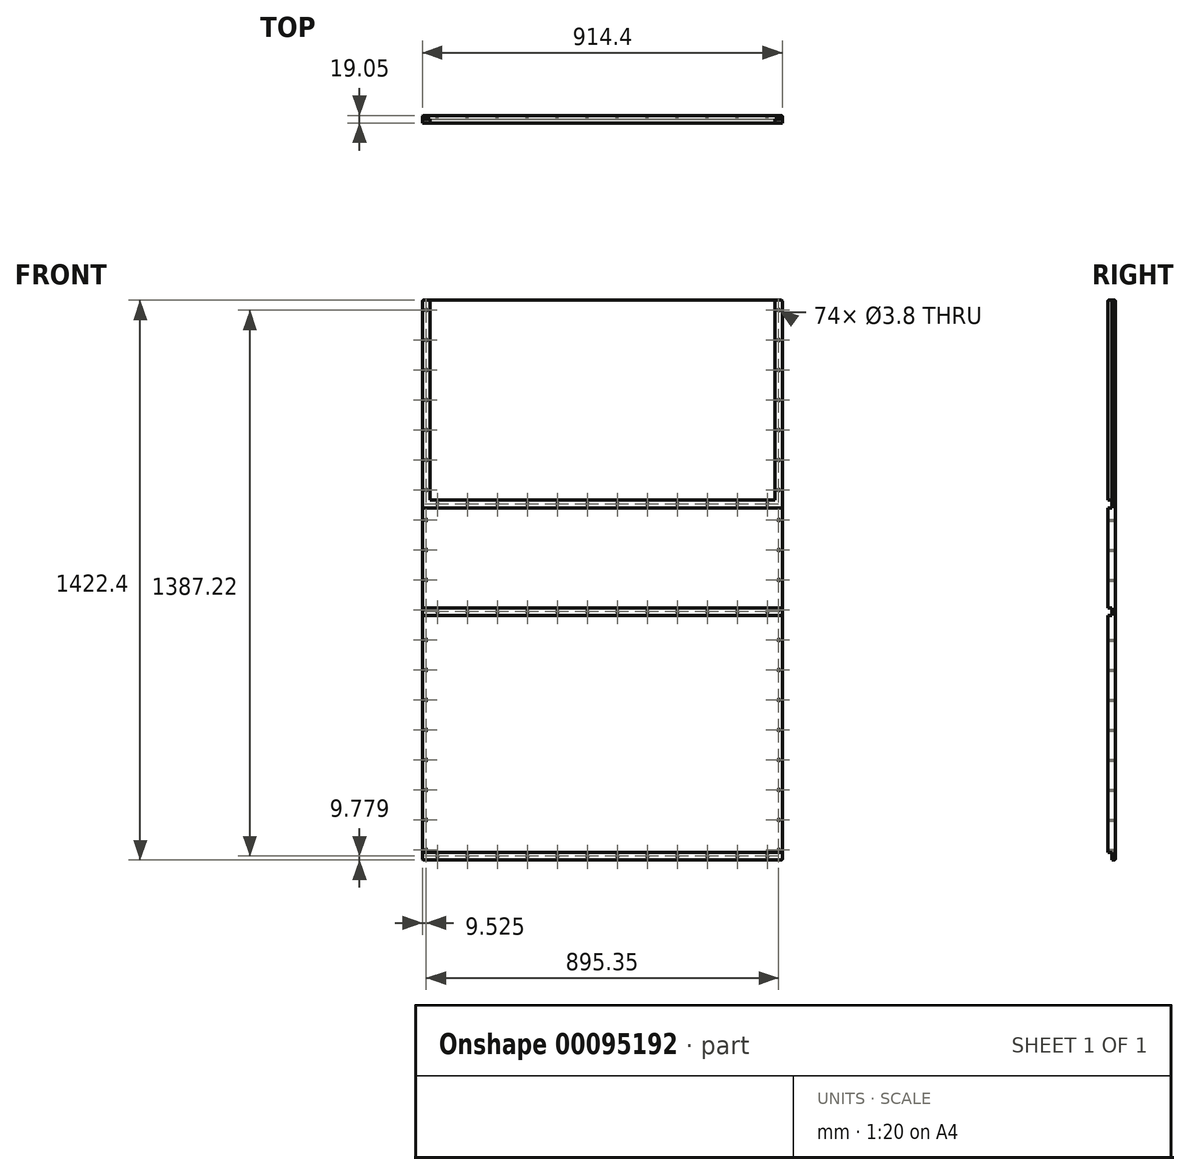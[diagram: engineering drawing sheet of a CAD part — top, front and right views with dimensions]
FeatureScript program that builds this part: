
annotation { "Feature Type Name" : "Feature", "Feature Type Description" : "" }
export const myFeature = defineFeature(function(context is Context, id is Id, definition is map)
    precondition{}
    {
        {
            var Q0;
            Q0=qCreatedBy(makeId("Front.planeOp"),FACE);
            var sketch = newSketch(context, id + "F0", { "sketchPlane" : qUnion([Q0])});
            skLineSegment(sketch, "E0.bottom", {"start": v(-457.2, -711.2) * mm, "end": v(457.2, -711.2) * mm});
            skLineSegment(sketch, "E0.top", {"start": v(-457.2, 711.2) * mm, "end": v(457.2, 711.2) * mm});
            skLineSegment(sketch, "E0.left", {"start": v(-457.2, -711.2) * mm, "end": v(-457.2, 711.2) * mm});
            skLineSegment(sketch, "E0.right", {"start": v(457.2, -711.2) * mm, "end": v(457.2, 711.2) * mm});
            skPoint(sketch, "E0.middle", {"position": v(0, 0) * mm});
            skSolve(sketch);
        }
        {
            var Q0;
            Q0=makeQuery(id+"F0.imprint","IMPRINT",FACE,{"disambiguationData":[TD([[makeQuery(id+"F0.imprint","IMPRINT",EDGE,{"derivedFrom":sQuery(id+"F0.wireOp",EDGE,"E0.bottom")}),1.0]])]});
            extrude(context, id + "F1", {"entities" : qUnion([Q0]), "depth" : 19.05 * mm});
        }
        {
            var Q0;
            Q0=makeQuery(id+"F1.opExtrude","CAP_FACE",FACE,{"disambiguationData":[OSD([sQuery(id+"F0.wireOp",EDGE,"E0.bottom"),sQuery(id+"F0.wireOp",EDGE,"E0.top"),sQuery(id+"F0.wireOp",EDGE,"E0.left"),sQuery(id+"F0.wireOp",EDGE,"E0.right")])],"isStart":false});
            var sketch = newSketch(context, id + "F2", { "sketchPlane" : qUnion([Q0])});
            skLineSegment(sketch, "E1", {"start": v(-457.2, 203.2) * mm, "end": v(457.2, 203.2) * mm, "construction": true});
            skLineSegment(sketch, "E2.bottom", {"start": v(-457.2, 203.2) * mm, "end": v(457.2, 203.2) * mm});
            skLineSegment(sketch, "E2.top", {"start": v(-457.2, 183.64) * mm, "end": v(457.2, 183.64) * mm});
            skLineSegment(sketch, "E2.left", {"start": v(-457.2, 203.2) * mm, "end": v(-457.2, 183.64) * mm});
            skLineSegment(sketch, "E2.right", {"start": v(457.2, 203.2) * mm, "end": v(457.2, 183.64) * mm});
            skLineSegment(sketch, "E3", {"start": v(-457.2, -691.64) * mm, "end": v(457.2, -691.64) * mm, "construction": true});
            skLineSegment(sketch, "E4.bottom", {"start": v(-457.2, -691.64) * mm, "end": v(457.2, -691.64) * mm});
            skLineSegment(sketch, "E4.top", {"start": v(-457.2, -711.2) * mm, "end": v(457.2, -711.2) * mm});
            skLineSegment(sketch, "E4.left", {"start": v(-457.2, -691.64) * mm, "end": v(-457.2, -711.2) * mm});
            skLineSegment(sketch, "E4.right", {"start": v(457.2, -691.64) * mm, "end": v(457.2, -711.2) * mm});
            skLineSegment(sketch, "E5", {"start": v(-457.2, 183.64) * mm, "end": v(-457.2, -70.36) * mm, "construction": true});
            skLineSegment(sketch, "E6.bottom", {"start": v(-457.2, -70.36) * mm, "end": v(457.2, -70.36) * mm});
            skLineSegment(sketch, "E6.top", {"start": v(-457.2, -89.92) * mm, "end": v(457.2, -89.92) * mm});
            skLineSegment(sketch, "E6.left", {"start": v(-457.2, -70.36) * mm, "end": v(-457.2, -89.92) * mm});
            skLineSegment(sketch, "E6.right", {"start": v(457.2, -70.36) * mm, "end": v(457.2, -89.92) * mm});
            skSolve(sketch);
        }
        {
            var Q0;
            Q0=makeQuery(id+"F2.imprint","IMPRINT",FACE,{"disambiguationData":[TD([[makeQuery(id+"F2.imprint","IMPRINT",EDGE,{"derivedFrom":sQuery(id+"F2.wireOp",EDGE,"E2.bottom")}),-1.0]])]});
            var Q1;
            Q1=makeQuery(id+"F2.imprint","IMPRINT",FACE,{"disambiguationData":[TD([[makeQuery(id+"F2.imprint","IMPRINT",EDGE,{"derivedFrom":sQuery(id+"F2.wireOp",EDGE,"E4.bottom")}),-1.0]])]});
            var Q2;
            Q2=makeQuery(id+"F2.imprint","IMPRINT",FACE,{"disambiguationData":[TD([[makeQuery(id+"F2.imprint","IMPRINT",EDGE,{"derivedFrom":sQuery(id+"F2.wireOp",EDGE,"E6.bottom")}),-1.0]])]});
            extrude(context, id + "F3", {"entities" : qUnion([Q0, Q1, Q2]), "operationType" : NewBodyOperationType.REMOVE, "oppositeDirection" : true, "depth" : 9.52 * mm});
        }
        {
            var Q0;
            Q0=makeQuery(id+"F1.opExtrude","CAP_FACE",FACE,{"disambiguationData":[OSD([sQuery(id+"F0.wireOp",EDGE,"E0.bottom"),sQuery(id+"F0.wireOp",EDGE,"E0.top"),sQuery(id+"F0.wireOp",EDGE,"E0.left"),sQuery(id+"F0.wireOp",EDGE,"E0.right")])],"isStart":true});
            var sketch = newSketch(context, id + "F4", { "sketchPlane" : qUnion([Q0])});
            skLineSegment(sketch, "E7.0", {"start": v(-457.2, -70.36) * mm, "end": v(-457.2, 183.64) * mm});
            skLineSegment(sketch, "E7.1", {"start": v(457.2, -89.92) * mm, "end": v(-457.2, -89.92) * mm});
            skLineSegment(sketch, "E7.2", {"start": v(457.2, 203.2) * mm, "end": v(-457.2, 203.2) * mm});
            skLineSegment(sketch, "E7.3", {"start": v(457.2, -70.36) * mm, "end": v(457.2, 183.64) * mm});
            skLineSegment(sketch, "E7.4", {"start": v(457.2, -70.36) * mm, "end": v(-457.2, -70.36) * mm});
            skLineSegment(sketch, "E7.5", {"start": v(457.2, 183.64) * mm, "end": v(-457.2, 183.64) * mm});
            skLineSegment(sketch, "E7.6", {"start": v(457.2, 183.64) * mm, "end": v(-457.2, 183.64) * mm});
            skLineSegment(sketch, "E7.7", {"start": v(457.2, -70.36) * mm, "end": v(-457.2, -70.36) * mm});
            skLineSegment(sketch, "E7.8", {"start": v(-457.2, -89.92) * mm, "end": v(-457.2, -70.36) * mm});
            skLineSegment(sketch, "E7.9", {"start": v(457.2, 203.2) * mm, "end": v(-457.2, 203.2) * mm});
            skLineSegment(sketch, "E7.10", {"start": v(457.2, -89.92) * mm, "end": v(457.2, -70.36) * mm});
            skLineSegment(sketch, "E7.11", {"start": v(457.2, -89.92) * mm, "end": v(-457.2, -89.92) * mm});
            skLineSegment(sketch, "E7.12", {"start": v(-457.2, 183.64) * mm, "end": v(-457.2, 203.2) * mm});
            skLineSegment(sketch, "E7.13", {"start": v(457.2, 183.64) * mm, "end": v(457.2, 203.2) * mm});
            skLineSegment(sketch, "E8.0", {"start": v(457.2, -691.64) * mm, "end": v(-457.2, -691.64) * mm});
            skLineSegment(sketch, "E8.1", {"start": v(457.2, -711.2) * mm, "end": v(-457.2, -711.2) * mm});
            skLineSegment(sketch, "E8.2", {"start": v(457.2, -711.2) * mm, "end": v(-457.2, -711.2) * mm});
            skLineSegment(sketch, "E8.3", {"start": v(457.2, -691.64) * mm, "end": v(-457.2, -691.64) * mm});
            skLineSegment(sketch, "E8.4", {"start": v(457.2, -711.2) * mm, "end": v(457.2, -691.64) * mm});
            skLineSegment(sketch, "E8.5", {"start": v(-457.2, -711.2) * mm, "end": v(-457.2, -691.64) * mm});
            skPoint(sketch, "E9", {"position": v(-419.1, -701.42) * mm});
            skPoint(sketch, "E9.positionSnap0", {"position": v(-457.2, -701.42) * mm});
            skPoint(sketch, "E10", {"position": v(-342.9, -701.42) * mm});
            skPoint(sketch, "E11", {"position": v(-266.7, -701.42) * mm});
            skPoint(sketch, "E12", {"position": v(-190.5, -701.42) * mm});
            skPoint(sketch, "E13", {"position": v(-114.3, -701.42) * mm});
            skPoint(sketch, "E14", {"position": v(-38.1, -701.42) * mm});
            skPoint(sketch, "E15", {"position": v(38.1, -701.42) * mm});
            skPoint(sketch, "E16", {"position": v(114.3, -701.42) * mm});
            skPoint(sketch, "E17", {"position": v(190.5, -701.42) * mm});
            skPoint(sketch, "E18", {"position": v(342.9, -701.42) * mm});
            skPoint(sketch, "E19", {"position": v(419.1, -701.42) * mm});
            skPoint(sketch, "E20", {"position": v(266.7, -701.42) * mm});
            skPoint(sketch, "E21", {"position": v(-419.1, -80.14) * mm});
            skPoint(sketch, "E21.positionSnap0", {"position": v(-457.2, -80.14) * mm});
            skPoint(sketch, "E22", {"position": v(-342.9, -80.14) * mm});
            skPoint(sketch, "E23", {"position": v(-266.7, -80.14) * mm});
            skPoint(sketch, "E24", {"position": v(-190.5, -80.14) * mm});
            skPoint(sketch, "E25", {"position": v(419.1, -80.14) * mm});
            skPoint(sketch, "E26", {"position": v(-114.3, -80.14) * mm});
            skPoint(sketch, "E27", {"position": v(-38.1, -80.14) * mm});
            skPoint(sketch, "E28", {"position": v(38.1, -80.14) * mm});
            skPoint(sketch, "E29", {"position": v(114.3, -80.14) * mm});
            skPoint(sketch, "E30", {"position": v(190.5, -80.14) * mm});
            skPoint(sketch, "E31", {"position": v(266.7, -80.14) * mm});
            skPoint(sketch, "E32", {"position": v(342.9, -80.14) * mm});
            skPoint(sketch, "E33", {"position": v(-457.2, 193.42) * mm});
            skPoint(sketch, "E34", {"position": v(-419.1, 193.42) * mm});
            skPoint(sketch, "E35", {"position": v(-342.9, 193.42) * mm});
            skPoint(sketch, "E36", {"position": v(-266.7, 193.42) * mm});
            skPoint(sketch, "E37", {"position": v(-190.5, 193.42) * mm});
            skPoint(sketch, "E38", {"position": v(-114.3, 193.42) * mm});
            skPoint(sketch, "E39", {"position": v(-38.1, 193.42) * mm});
            skPoint(sketch, "E40", {"position": v(38.1, 193.42) * mm});
            skPoint(sketch, "E41", {"position": v(114.3, 193.42) * mm});
            skPoint(sketch, "E42", {"position": v(190.5, 193.42) * mm});
            skPoint(sketch, "E43", {"position": v(266.7, 193.42) * mm});
            skPoint(sketch, "E44", {"position": v(342.9, 193.42) * mm});
            skPoint(sketch, "E45", {"position": v(419.1, 193.42) * mm});
            skSolve(sketch);
        }
        {
            var Q0;
            Q0=sQuery(id+"F4.wireOp",VERTEX,"E9");
            var Q1;
            Q1=sQuery(id+"F4.wireOp",VERTEX,"E10");
            var Q2;
            Q2=sQuery(id+"F4.wireOp",VERTEX,"E11");
            var Q3;
            Q3=sQuery(id+"F4.wireOp",VERTEX,"E12");
            var Q4;
            Q4=sQuery(id+"F4.wireOp",VERTEX,"E13");
            var Q5;
            Q5=sQuery(id+"F4.wireOp",VERTEX,"E14");
            var Q6;
            Q6=sQuery(id+"F4.wireOp",VERTEX,"E15");
            var Q7;
            Q7=sQuery(id+"F4.wireOp",VERTEX,"E16");
            var Q8;
            Q8=sQuery(id+"F4.wireOp",VERTEX,"E17");
            var Q9;
            Q9=sQuery(id+"F4.wireOp",VERTEX,"E20");
            var Q10;
            Q10=sQuery(id+"F4.wireOp",VERTEX,"E18");
            var Q11;
            Q11=sQuery(id+"F4.wireOp",VERTEX,"E19");
            var Q12;
            Q12=sQuery(id+"F4.wireOp",VERTEX,"E32");
            var Q13;
            Q13=sQuery(id+"F4.wireOp",VERTEX,"E27");
            var Q14;
            Q14=sQuery(id+"F4.wireOp",VERTEX,"E28");
            var Q15;
            Q15=sQuery(id+"F4.wireOp",VERTEX,"E23");
            var Q16;
            Q16=sQuery(id+"F4.wireOp",VERTEX,"E21");
            var Q17;
            Q17=sQuery(id+"F4.wireOp",VERTEX,"E29");
            var Q18;
            Q18=sQuery(id+"F4.wireOp",VERTEX,"E25");
            var Q19;
            Q19=sQuery(id+"F4.wireOp",VERTEX,"E30");
            var Q20;
            Q20=sQuery(id+"F4.wireOp",VERTEX,"E26");
            var Q21;
            Q21=sQuery(id+"F4.wireOp",VERTEX,"E22");
            var Q22;
            Q22=sQuery(id+"F4.wireOp",VERTEX,"E31");
            var Q23;
            Q23=sQuery(id+"F4.wireOp",VERTEX,"E24");
            var Q24;
            Q24=sQuery(id+"F4.wireOp",VERTEX,"E43");
            var Q25;
            Q25=sQuery(id+"F4.wireOp",VERTEX,"E41");
            var Q26;
            Q26=sQuery(id+"F4.wireOp",VERTEX,"E44");
            var Q27;
            Q27=sQuery(id+"F4.wireOp",VERTEX,"E35");
            var Q28;
            Q28=sQuery(id+"F4.wireOp",VERTEX,"E39");
            var Q29;
            Q29=sQuery(id+"F4.wireOp",VERTEX,"E36");
            var Q30;
            Q30=sQuery(id+"F4.wireOp",VERTEX,"E45");
            var Q31;
            Q31=sQuery(id+"F4.wireOp",VERTEX,"E34");
            var Q32;
            Q32=sQuery(id+"F4.wireOp",VERTEX,"E40");
            var Q33;
            Q33=sQuery(id+"F4.wireOp",VERTEX,"E37");
            var Q34;
            Q34=sQuery(id+"F4.wireOp",VERTEX,"E42");
            var Q35;
            Q35=sQuery(id+"F4.wireOp",VERTEX,"E38");
            var Q36;
            Q36=makeQuery(id+"F1.opExtrude","SWEPT_BODY",BODY,{"disambiguationData":[OSD([sQuery(id+"F0.wireOp",EDGE,"E0.bottom"),sQuery(id+"F0.wireOp",EDGE,"E0.top"),sQuery(id+"F0.wireOp",EDGE,"E0.left"),sQuery(id+"F0.wireOp",EDGE,"E0.right")])]});
            hole(context, id + "F5", {"style" : HoleStyle.C_SINK, "endStyle" : HoleEndStyle.THROUGH, "standardTappedOrClearance" : lookupTablePath({ "standard" : "ANSI", "fit" : "Normal (ASME)", "size" : "#6", "type" : "Clearance" }), "standardBlindInLast" : lookupTablePath({ "fit" : "Free", "standard" : "ANSI", "size" : "#6", "type" : "Clearance" }), "holeDiameter" : 3.8 * mm, "cSinkDiameter" : 7.8 * mm, "cSinkAngle" : 82 * degree, "startFromSketch" : true, "locations" : qUnion([Q0, Q1, Q2, Q3, Q4, Q5, Q6, Q7, Q8, Q9, Q10, Q11, Q12, Q13, Q14, Q15, Q16, Q17, Q18, Q19, Q20, Q21, Q22, Q23, Q24, Q25, Q26, Q27, Q28, Q29, Q30, Q31, Q32, Q33, Q34, Q35]), "scope" : qUnion([Q36]), "isTappedThrough" : true});
        }
        {
            var Q0;
            {var subQ0=sQuery(id+"F0.wireOp",EDGE,"E0.top");var subQ1=sQuery(id+"F0.wireOp",EDGE,"E0.left");var subQ2=sQuery(id+"F0.wireOp",EDGE,"E0.right");Q0=makeQuery(id+"F3.boolean.opBoolean","SPLIT",FACE,{"disambiguationData":[TD([makeQuery(id+"F1.opExtrude","SWEPT_FACE",FACE,{"disambiguationData":[OSD([subQ0])]})])],"derivedFrom":makeQuery(id+"F1.opExtrude","CAP_FACE",FACE,{"disambiguationData":[OSD([sQuery(id+"F0.wireOp",EDGE,"E0.bottom"),subQ0,subQ1,subQ2])],"isStart":false})});}
            var sketch = newSketch(context, id + "F6", { "sketchPlane" : qUnion([Q0])});
            skLineSegment(sketch, "E46.0", {"start": v(-457.2, -691.64) * mm, "end": v(457.2, -691.64) * mm});
            skLineSegment(sketch, "E47.bottom", {"start": v(-457.2, 711.2) * mm, "end": v(-438.15, 711.2) * mm});
            skLineSegment(sketch, "E47.top", {"start": v(-457.2, -691.64) * mm, "end": v(-438.15, -691.64) * mm});
            skLineSegment(sketch, "E47.left", {"start": v(-457.2, 711.2) * mm, "end": v(-457.2, -691.64) * mm});
            skLineSegment(sketch, "E47.right", {"start": v(-438.15, 711.2) * mm, "end": v(-438.15, -691.64) * mm});
            skLineSegment(sketch, "E48.bottom", {"start": v(457.2, 711.2) * mm, "end": v(438.15, 711.2) * mm});
            skLineSegment(sketch, "E48.top", {"start": v(457.2, -691.64) * mm, "end": v(438.15, -691.64) * mm});
            skLineSegment(sketch, "E48.left", {"start": v(457.2, 711.2) * mm, "end": v(457.2, -691.64) * mm});
            skLineSegment(sketch, "E48.right", {"start": v(438.15, 711.2) * mm, "end": v(438.15, -691.64) * mm});
            skSolve(sketch);
        }
        {
            var Q0;
            {var subQ0=sQuery(id+"F6.wireOp",EDGE,"E47.bottom");Q0=makeQuery(id+"F6.imprint","IMPRINT",FACE,{"disambiguationData":[TD([[makeQuery(id+"F6.imprint","IMPRINT",EDGE,{"derivedFrom":subQ0}),-1.0]])]});}
            var Q1;
            {var subQ0=sQuery(id+"F6.wireOp",EDGE,"E48.bottom");Q1=makeQuery(id+"F6.imprint","IMPRINT",FACE,{"disambiguationData":[TD([[makeQuery(id+"F6.imprint","IMPRINT",EDGE,{"derivedFrom":subQ0}),-1.0]])]});}
            var Q2;
            {var subQ0=sQuery(id+"F6.wireOp",EDGE,"E48.top");Q2=makeQuery(id+"F6.imprint","IMPRINT",FACE,{"disambiguationData":[TD([[makeQuery(id+"F6.imprint","IMPRINT",EDGE,{"derivedFrom":subQ0}),-1.0]])]});}
            var Q3;
            {var subQ0=sQuery(id+"F6.wireOp",EDGE,"E47.top");Q3=makeQuery(id+"F6.imprint","IMPRINT",FACE,{"disambiguationData":[TD([[makeQuery(id+"F6.imprint","IMPRINT",EDGE,{"derivedFrom":subQ0}),1.0]])]});}
            extrude(context, id + "F7", {"entities" : qUnion([Q0, Q1, Q2, Q3]), "operationType" : NewBodyOperationType.REMOVE, "oppositeDirection" : true, "depth" : 9.52 * mm});
        }
        {
            var Q0;
            Q0=makeQuery(id+"F1.opExtrude","CAP_FACE",FACE,{"disambiguationData":[OSD([sQuery(id+"F0.wireOp",EDGE,"E0.bottom"),sQuery(id+"F0.wireOp",EDGE,"E0.top"),sQuery(id+"F0.wireOp",EDGE,"E0.left"),sQuery(id+"F0.wireOp",EDGE,"E0.right")])],"isStart":true});
            var sketch = newSketch(context, id + "F8", { "sketchPlane" : qUnion([Q0])});
            skLineSegment(sketch, "E49.0", {"start": v(-438.15, 711.2) * mm, "end": v(-457.2, 711.2) * mm});
            skLineSegment(sketch, "E50.0", {"start": v(457.2, 711.2) * mm, "end": v(438.15, 711.2) * mm});
            skPoint(sketch, "E51", {"position": v(-447.68, 685.8) * mm});
            skPoint(sketch, "E51.positionSnap0", {"position": v(-447.68, 711.2) * mm});
            skPoint(sketch, "E52", {"position": v(-447.68, 609.6) * mm});
            skPoint(sketch, "E53", {"position": v(-447.68, 533.4) * mm});
            skPoint(sketch, "E54", {"position": v(-447.68, 457.2) * mm});
            skPoint(sketch, "E55", {"position": v(-447.68, 381) * mm});
            skPoint(sketch, "E56", {"position": v(-447.68, 228.6) * mm});
            skPoint(sketch, "E57", {"position": v(-447.68, 152.4) * mm});
            skPoint(sketch, "E58", {"position": v(-447.68, -76.2) * mm});
            skPoint(sketch, "E59", {"position": v(-447.68, -152.4) * mm});
            skPoint(sketch, "E60", {"position": v(-447.68, -381) * mm});
            skPoint(sketch, "E61", {"position": v(-447.68, -457.2) * mm});
            skPoint(sketch, "E62", {"position": v(-447.68, -533.4) * mm});
            skPoint(sketch, "E63", {"position": v(-447.68, 304.8) * mm});
            skPoint(sketch, "E64", {"position": v(-447.68, 76.2) * mm});
            skPoint(sketch, "E65", {"position": v(-447.68, 0) * mm});
            skPoint(sketch, "E66", {"position": v(-447.68, -228.6) * mm});
            skPoint(sketch, "E67", {"position": v(-447.68, -304.8) * mm});
            skPoint(sketch, "E68", {"position": v(-447.68, -609.6) * mm});
            skPoint(sketch, "E69", {"position": v(-447.68, -685.8) * mm});
            skLineSegment(sketch, "E70", {"start": v(0, 711.2) * mm, "end": v(0, -711.2) * mm, "construction": true});
            skPoint(sketch, "E71.MirrorP", {"position": v(447.68, 609.6) * mm});
            skPoint(sketch, "E72.MirrorP", {"position": v(447.68, 533.4) * mm});
            skPoint(sketch, "E73.MirrorP", {"position": v(447.67, 685.8) * mm});
            skPoint(sketch, "E74.MirrorP", {"position": v(447.68, 381) * mm});
            skPoint(sketch, "E75.MirrorP", {"position": v(447.68, 457.2) * mm});
            skPoint(sketch, "E76.MirrorP", {"position": v(447.68, -228.6) * mm});
            skPoint(sketch, "E77.MirrorP", {"position": v(447.68, -457.2) * mm});
            skPoint(sketch, "E78.MirrorP", {"position": v(447.68, 304.8) * mm});
            skPoint(sketch, "E79.MirrorP", {"position": v(447.68, -304.8) * mm});
            skPoint(sketch, "E80.MirrorP", {"position": v(447.68, -381) * mm});
            skPoint(sketch, "E81.MirrorP", {"position": v(447.68, 0) * mm});
            skPoint(sketch, "E82.MirrorP", {"position": v(447.68, -152.4) * mm});
            skPoint(sketch, "E83.MirrorP", {"position": v(447.68, 152.4) * mm});
            skPoint(sketch, "E84.MirrorP", {"position": v(447.68, -76.2) * mm});
            skPoint(sketch, "E85.MirrorP", {"position": v(447.68, 228.6) * mm});
            skPoint(sketch, "E86.MirrorP", {"position": v(447.68, 76.2) * mm});
            skPoint(sketch, "E87.MirrorP", {"position": v(447.68, -685.8) * mm});
            skPoint(sketch, "E88.MirrorP", {"position": v(447.68, -609.6) * mm});
            skPoint(sketch, "E89.MirrorP", {"position": v(447.68, -533.4) * mm});
            skSolve(sketch);
        }
        {
            var Q0;
            Q0=sQuery(id+"F8.wireOp",VERTEX,"E57");
            var Q1;
            Q1=sQuery(id+"F8.wireOp",VERTEX,"E58");
            var Q2;
            Q2=sQuery(id+"F8.wireOp",VERTEX,"E59");
            var Q3;
            Q3=sQuery(id+"F8.wireOp",VERTEX,"E65");
            var Q4;
            Q4=sQuery(id+"F8.wireOp",VERTEX,"E68");
            var Q5;
            Q5=sQuery(id+"F8.wireOp",VERTEX,"E55");
            var Q6;
            Q6=sQuery(id+"F8.wireOp",VERTEX,"E54");
            var Q7;
            Q7=sQuery(id+"F8.wireOp",VERTEX,"E62");
            var Q8;
            Q8=sQuery(id+"F8.wireOp",VERTEX,"E56");
            var Q9;
            Q9=sQuery(id+"F8.wireOp",VERTEX,"E51");
            var Q10;
            Q10=sQuery(id+"F8.wireOp",VERTEX,"E64");
            var Q11;
            Q11=sQuery(id+"F8.wireOp",VERTEX,"E63");
            var Q12;
            Q12=sQuery(id+"F8.wireOp",VERTEX,"E53");
            var Q13;
            Q13=sQuery(id+"F8.wireOp",VERTEX,"E60");
            var Q14;
            Q14=sQuery(id+"F8.wireOp",VERTEX,"E52");
            var Q15;
            Q15=sQuery(id+"F8.wireOp",VERTEX,"E67");
            var Q16;
            Q16=sQuery(id+"F8.wireOp",VERTEX,"E61");
            var Q17;
            Q17=sQuery(id+"F8.wireOp",VERTEX,"E66");
            var Q18;
            Q18=sQuery(id+"F8.wireOp",VERTEX,"E69");
            var Q19;
            Q19=sQuery(id+"F8.wireOp",VERTEX,"E71.MirrorP");
            var Q20;
            Q20=sQuery(id+"F8.wireOp",VERTEX,"E82.MirrorP");
            var Q21;
            Q21=sQuery(id+"F8.wireOp",VERTEX,"E75.MirrorP");
            var Q22;
            Q22=sQuery(id+"F8.wireOp",VERTEX,"E87.MirrorP");
            var Q23;
            Q23=sQuery(id+"F8.wireOp",VERTEX,"E85.MirrorP");
            var Q24;
            Q24=sQuery(id+"F8.wireOp",VERTEX,"E73.MirrorP");
            var Q25;
            Q25=sQuery(id+"F8.wireOp",VERTEX,"E79.MirrorP");
            var Q26;
            Q26=sQuery(id+"F8.wireOp",VERTEX,"E81.MirrorP");
            var Q27;
            Q27=sQuery(id+"F8.wireOp",VERTEX,"E74.MirrorP");
            var Q28;
            Q28=sQuery(id+"F8.wireOp",VERTEX,"E72.MirrorP");
            var Q29;
            Q29=sQuery(id+"F8.wireOp",VERTEX,"E89.MirrorP");
            var Q30;
            Q30=sQuery(id+"F8.wireOp",VERTEX,"E80.MirrorP");
            var Q31;
            Q31=sQuery(id+"F8.wireOp",VERTEX,"E77.MirrorP");
            var Q32;
            Q32=sQuery(id+"F8.wireOp",VERTEX,"E78.MirrorP");
            var Q33;
            Q33=sQuery(id+"F8.wireOp",VERTEX,"E86.MirrorP");
            var Q34;
            Q34=sQuery(id+"F8.wireOp",VERTEX,"E83.MirrorP");
            var Q35;
            Q35=sQuery(id+"F8.wireOp",VERTEX,"E76.MirrorP");
            var Q36;
            Q36=sQuery(id+"F8.wireOp",VERTEX,"E88.MirrorP");
            var Q37;
            Q37=sQuery(id+"F8.wireOp",VERTEX,"E84.MirrorP");
            var Q38;
            Q38=makeQuery(id+"F1.opExtrude","SWEPT_BODY",BODY,{"disambiguationData":[OSD([sQuery(id+"F0.wireOp",EDGE,"E0.bottom"),sQuery(id+"F0.wireOp",EDGE,"E0.top"),sQuery(id+"F0.wireOp",EDGE,"E0.left"),sQuery(id+"F0.wireOp",EDGE,"E0.right")])]});
            hole(context, id + "F9", {"style" : HoleStyle.C_SINK, "endStyle" : HoleEndStyle.THROUGH, "standardTappedOrClearance" : lookupTablePath({ "standard" : "ANSI", "fit" : "Normal (ASME)", "size" : "#6", "type" : "Clearance" }), "standardBlindInLast" : lookupTablePath({ "fit" : "Free", "standard" : "ANSI", "size" : "#6", "type" : "Clearance" }), "holeDiameter" : 3.8 * mm, "cSinkDiameter" : 7.8 * mm, "cSinkAngle" : 82 * degree, "startFromSketch" : true, "locations" : qUnion([Q0, Q1, Q2, Q3, Q4, Q5, Q6, Q7, Q8, Q9, Q10, Q11, Q12, Q13, Q14, Q15, Q16, Q17, Q18, Q19, Q20, Q21, Q22, Q23, Q24, Q25, Q26, Q27, Q28, Q29, Q30, Q31, Q32, Q33, Q34, Q35, Q36, Q37]), "scope" : qUnion([Q38]), "isTappedThrough" : true});
        }
        {
            var Q0;
            Q0=makeQuery(id+"F1.opExtrude","CAP_EDGE",EDGE,{"disambiguationData":[OSD([sQuery(id+"F0.wireOp",EDGE,"E0.right")])],"isStart":true});
            var Q1;
            Q1=makeQuery(id+"F1.opExtrude","CAP_EDGE",EDGE,{"disambiguationData":[OSD([sQuery(id+"F0.wireOp",EDGE,"E0.top")])],"isStart":true});
            var Q2;
            Q2=makeQuery(id+"F1.opExtrude","CAP_EDGE",EDGE,{"disambiguationData":[OSD([sQuery(id+"F0.wireOp",EDGE,"E0.left")])],"isStart":true});
            var Q3;
            Q3=makeQuery(id+"F1.opExtrude","CAP_EDGE",EDGE,{"disambiguationData":[OSD([sQuery(id+"F0.wireOp",EDGE,"E0.bottom")])],"isStart":true});
            var Q4;
            Q4=makeQuery(id+"F1.opExtrude","SWEPT_EDGE",EDGE,{"disambiguationData":[OSD([sQuery(id+"F0.wireOp",EDGE,"E0.bottom"),sQuery(id+"F0.wireOp",EDGE,"E0.right")])]});
            var Q5;
            Q5=makeQuery(id+"F1.opExtrude","SWEPT_EDGE",EDGE,{"disambiguationData":[OSD([sQuery(id+"F0.wireOp",EDGE,"E0.bottom"),sQuery(id+"F0.wireOp",EDGE,"E0.left")])]});
            var Q6;
            Q6=makeQuery(id+"F1.opExtrude","SWEPT_EDGE",EDGE,{"disambiguationData":[OSD([sQuery(id+"F0.wireOp",EDGE,"E0.top"),sQuery(id+"F0.wireOp",EDGE,"E0.left")])]});
            var Q7;
            Q7=makeQuery(id+"F1.opExtrude","SWEPT_EDGE",EDGE,{"disambiguationData":[OSD([sQuery(id+"F0.wireOp",EDGE,"E0.top"),sQuery(id+"F0.wireOp",EDGE,"E0.right")])]});
            var Q8;
            Q8=makeQuery(id+"F1.opExtrude","CAP_EDGE",EDGE,{"disambiguationData":[OSD([sQuery(id+"F0.wireOp",EDGE,"E0.top")])],"isStart":false});
            fillet(context, id + "F10", {"entities" : qUnion([Q0, Q1, Q2, Q3, Q4, Q5, Q6, Q7, Q8]), "radius" : 3.17 * mm, "tangentPropagation" : true, "allowEdgeOverflow" : false});
        }
    });
